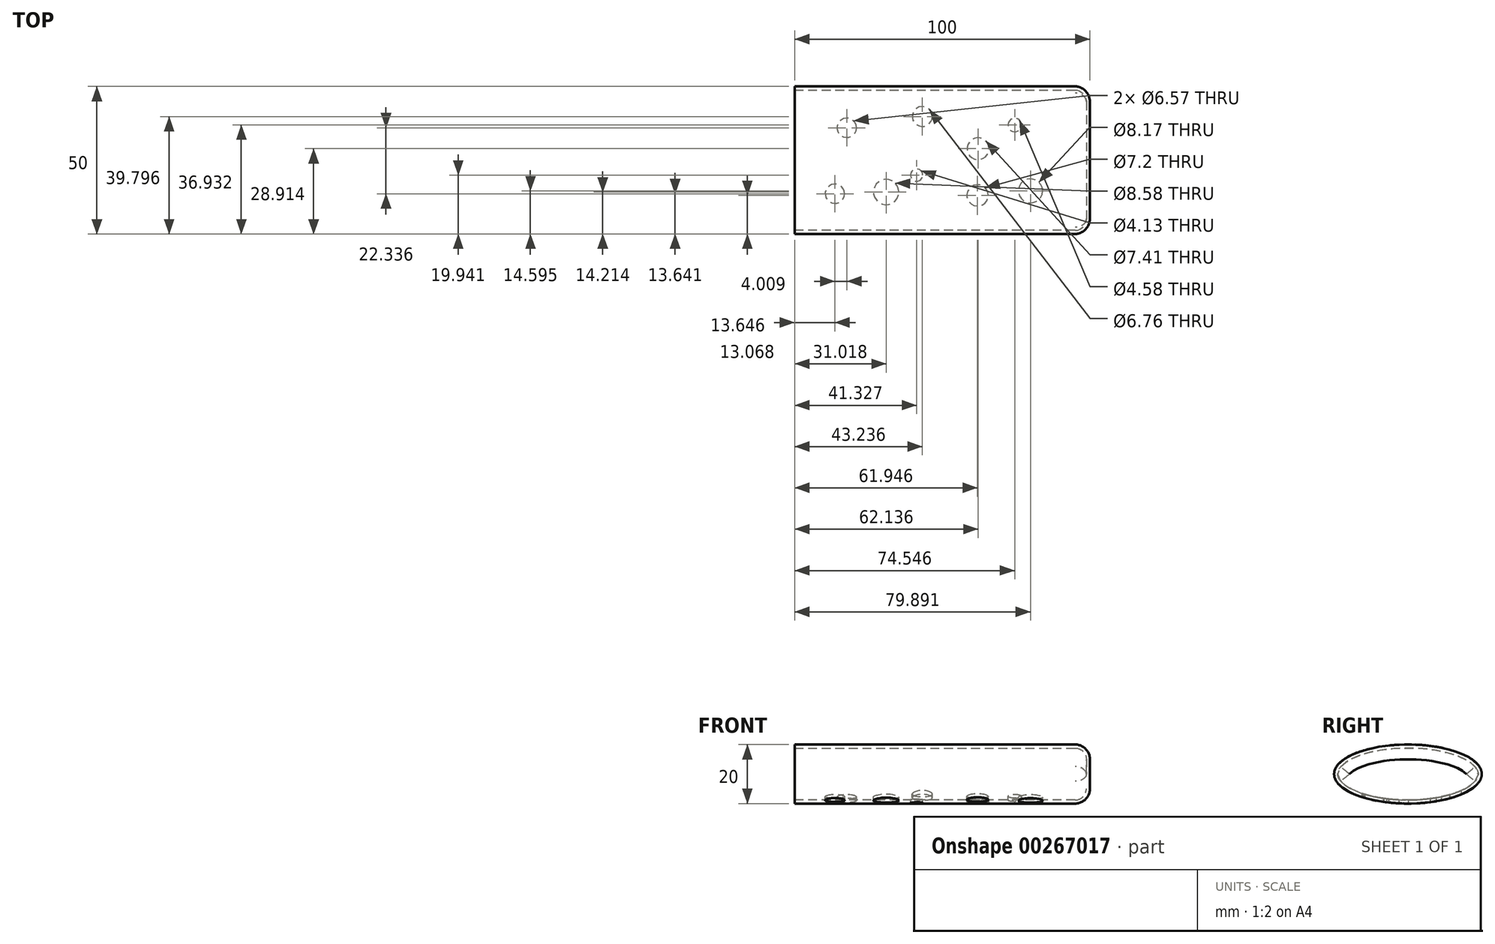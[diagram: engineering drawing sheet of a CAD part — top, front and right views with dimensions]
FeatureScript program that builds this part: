
annotation { "Feature Type Name" : "Feature", "Feature Type Description" : "" }
export const myFeature = defineFeature(function(context is Context, id is Id, definition is map)
    precondition{}
    {
        {
            var Q0;
            Q0=qCreatedBy(makeId("Right.planeOp"),FACE);
            var sketch = newSketch(context, id + "F0", { "sketchPlane" : qUnion([Q0])});
            skEllipse(sketch, "E0", {"center": v(0, 0) * mm, "majorRadius": 25 * mm, "minorRadius": 10 * mm, "majorAxis": v(1, 0)});
            skSolve(sketch);
        }
        {
            var Q0;
            Q0 = qSketchRegion(id + "F0", true);
            extrude(context, id + "F1", {"entities" : qUnion([Q0]), "depth" : 100 * mm});
        }
        {
            var Q0;
            Q0=makeQuery(id+"F1.opExtrude","CAP_EDGE",EDGE,{"disambiguationData":[OSD([sQuery(id+"F0.wireOp",EDGE,"E0")])],"isStart":false});
            fillet(context, id + "F2", {"entities" : qUnion([Q0]), "radius" : 5 * mm, "tangentPropagation" : true, "allowEdgeOverflow" : false});
        }
        {
            var Q0;
            Q0=makeQuery(id+"F1.opExtrude","CAP_FACE",FACE,{"disambiguationData":[OSD([sQuery(id+"F0.wireOp",EDGE,"E0")])],"isStart":true});
            shell(context, id + "F3", {"entities" : qUnion([Q0]), "thickness" : 1.2 * mm});
        }
        {
            var Q0;
            Q0=qCreatedBy(makeId("Top.planeOp"),FACE);
            var sketch = newSketch(context, id + "F4", { "sketchPlane" : qUnion([Q0])});
            skCircle(sketch, "E1", {"center": v(17.65, 10.98) * mm, "radius": 3.28 * mm});
            skCircle(sketch, "E2", {"center": v(43.24, 14.8) * mm, "radius": 3.38 * mm});
            skCircle(sketch, "E3", {"center": v(74.55, 11.93) * mm, "radius": 2.3 * mm});
            skCircle(sketch, "E4", {"center": v(62.14, 3.91) * mm, "radius": 3.7 * mm});
            skCircle(sketch, "E5", {"center": v(41.33, -5.06) * mm, "radius": 2.06 * mm});
            skCircle(sketch, "E6", {"center": v(31.02, -10.79) * mm, "radius": 4.3 * mm});
            skCircle(sketch, "E7", {"center": v(13.65, -11.36) * mm, "radius": 3.28 * mm});
            skCircle(sketch, "E8", {"center": v(61.95, -11.93) * mm, "radius": 3.6 * mm});
            skCircle(sketch, "E9", {"center": v(79.9, -10.4) * mm, "radius": 4.09 * mm});
            skSolve(sketch);
        }
        {
            var Q0;
            Q0 = qSketchRegion(id + "F4", true);
            extrude(context, id + "F5", {"entities" : qUnion([Q0]), "operationType" : NewBodyOperationType.REMOVE, "oppositeDirection" : true, "depth" : 25 * mm});
        }
    });
